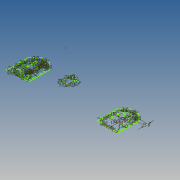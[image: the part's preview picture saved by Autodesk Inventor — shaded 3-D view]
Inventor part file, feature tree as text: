
AUTODESK INVENTOR PART (.ipt)
format: ipt  version: 2014 (Build 180170000, 170)  size: 240,640 bytes
history: native  units: mm
features: sketch x2
ambient origin geometry x8: Origin, YZ Plane, XZ Plane, XY Plane, X Axis, Y Axis, Z Axis, Center Point
feature tree (2):
  sketch  "Sketch1"  dims[d12=10.0mm d13=2.0mm d16=10.0mm d17=2.0mm d19=10.0mm d20=2.0mm d23=10.0mm d24=2.0mm d25=10.0mm d26=10.0mm d27=2.0mm d28=10.0mm d29=2.0mm d30=10.0mm d33=15.0mm d34=2.0mm d36=15.0mm d37=18.0mm d38=15.0mm d39=17.0mm d40=2.0mm d41=15.0mm d43=15.0mm d44=18.0mm d45=15.0mm d46=17.0mm d47=15.0mm d48=18.0mm d52=15.0mm d54=18.0mm d55=219.764931mm d56=174.51mm d57=3.0mm d58=3.0mm d59=3.0mm d60=3.0mm d61=3.0mm d62=-5.117mm d63=10.0mm d64=15.117mm d65=10.0mm d66=5.554212mm d67=5.0mm d68=5.0mm d69=5.554212mm d70=5.554212mm d71=5.0mm d72=5.0mm d75=3.0mm d76=3.0mm d77=3.0mm d78=5.117mm d79=0.0mm d80=15.117007mm d81=3.0mm d82=5.0mm d83=5.0mm d84=5.0mm d85=5.000007mm d86=5.0mm d94=57.0mm d95=67.0mm d96=3.0mm d97=3.0mm d98=3.0mm d99=51.0mm d100=51.0mm d101=51.0mm d102=51.0mm d103=3.0mm d104=2.0mm d105=12.0mm d106=12.0mm d107=11.0mm d108=11.0mm d109=3.0mm d110=3.0mm d111=3.0mm d112=2.0mm d113=12.0mm d114=12.0mm d116=11.0mm d118=3.0mm d121=3.0mm d124=10.0mm d125=2.0mm d126=10.0mm d127=2.0mm d128=10.0mm d129=2.0mm d130=10.0mm d131=2.0mm d132=10.0mm d133=10.0mm d134=2.0mm d135=10.0mm d136=2.0mm d137=10.0mm d138=15.0mm d139=2.0mm d140=15.0mm d141=18.0mm d142=15.0mm d143=17.0mm d144=2.0mm d145=15.0mm d146=15.0mm d147=18.0mm d148=15.0mm d149=17.0mm d150=15.0mm d151=18.0mm d152=15.0mm d153=18.0mm d154=219.764931mm d155=174.51mm d156=3.0mm d157=3.0mm d158=71.8mm d159=25.8mm d160=35.0mm d161=16.0mm d163=25.0mm d164=13.0mm d165=21.0mm d166=40.0mm d167=9.7mm d168=20.0mm d203=3.0mm d204=3.0mm d205=95.933639mm d206=95.933639mm d207=95.933639mm d208=50.0mm d211=60.0mm d212=5.0mm d213=110.0mm d214=20.0mm d216=10.0mm d217=5.0mm d248=27.4mm d249=40.4mm d250=3.0mm d251=3.0mm d252=23.7mm d253=39.8mm d254=30.0mm d255=30.0mm d256=5.0mm]
  sketch  "Sketch2"
